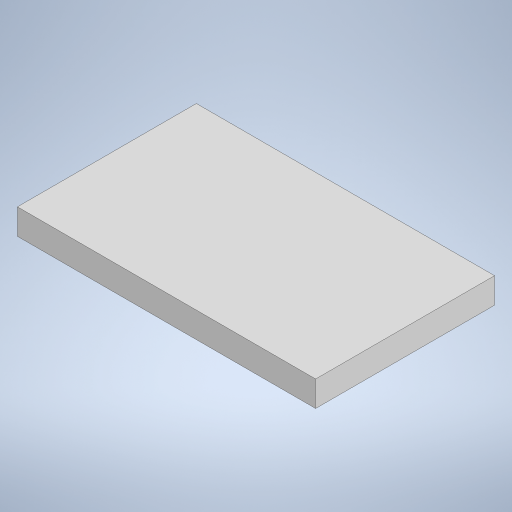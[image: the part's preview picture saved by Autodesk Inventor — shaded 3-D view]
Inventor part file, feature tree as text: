
AUTODESK INVENTOR PART (.ipt)
format: ipt  version: 2023 (Build 270158000, 158)  size: 195,584 bytes
history: native  units: in
note: dims shown in document units (in); Inventor stores cm internally (conversion verified against a paired STEP export)
features: extrude x1, sketch x1
ambient origin geometry x8: Origin, YZ Plane, XZ Plane, XY Plane, X Axis, Y Axis, Z Axis, Center Point
bodies: Solid1 (feature_tree)
feature tree (2):
  extrude  "Extrusion1"  Depth=2.1in
  sketch  "Sketch1"  dims[d0=3.5in d1=2.1in d2=0.3in d3=0.0in]
